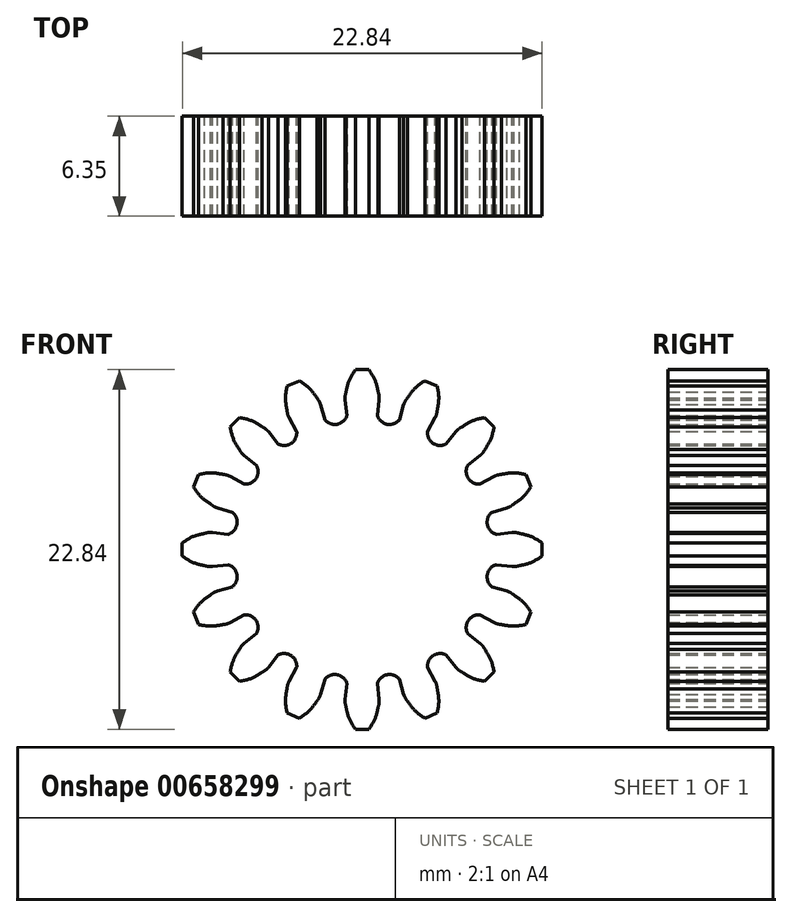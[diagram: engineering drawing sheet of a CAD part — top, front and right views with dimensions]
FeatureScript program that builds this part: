
annotation { "Feature Type Name" : "Feature", "Feature Type Description" : "" }
export const myFeature = defineFeature(function(context is Context, id is Id, definition is map)
    precondition{}
    {
        {
            var Q0;
            Q0=qCreatedBy(makeId("Front.planeOp"),FACE);
            var sketch = newSketch(context, id + "F0", { "sketchPlane" : qUnion([Q0])});
            skLineSegment(sketch, "E0", {"start": v(8.52, -0.97) * mm, "end": v(9.5, -1.08) * mm});
            skFitSpline(sketch, "E1", {"points": [v(9.5, -1.08) * mm, v(9.56, -1.08) * mm, v(9.73, -1.08) * mm, v(10, -1.02) * mm]});
            skFitSpline(sketch, "E2", {"points": [v(10, -1.02) * mm, v(10.34, -0.95) * mm, v(10.83, -0.78) * mm, v(11.42, -0.42) * mm]});
            skLineSegment(sketch, "E3", {"start": v(11.42, -0.42) * mm, "end": v(11.42, 0.42) * mm});
            skFitSpline(sketch, "E4", {"points": [v(11.42, 0.42) * mm, v(10.83, 0.78) * mm, v(10.34, 0.95) * mm, v(10, 1.02) * mm]});
            skFitSpline(sketch, "E5", {"points": [v(10, 1.02) * mm, v(9.73, 1.08) * mm, v(9.56, 1.08) * mm, v(9.5, 1.08) * mm]});
            skLineSegment(sketch, "E6", {"start": v(9.5, 1.08) * mm, "end": v(8.52, 0.97) * mm});
            skArc(sketch, "E7", {"start": v(8.24, 2.37) * mm, "mid": v(7.95, 1.58) * mm, "end": v(8.52, 0.97) * mm});
            skLineSegment(sketch, "E8", {"start": v(8.24, 2.37) * mm, "end": v(9.2, 2.64) * mm});
            skFitSpline(sketch, "E9", {"points": [v(9.2, 2.64) * mm, v(9.25, 2.66) * mm, v(9.4, 2.72) * mm, v(9.63, 2.88) * mm]});
            skFitSpline(sketch, "E10", {"points": [v(9.63, 2.88) * mm, v(9.91, 3.08) * mm, v(10.3, 3.42) * mm, v(10.72, 3.98) * mm]});
            skLineSegment(sketch, "E11", {"start": v(10.72, 3.98) * mm, "end": v(10.4, 4.76) * mm});
            skFitSpline(sketch, "E12", {"points": [v(10.4, 4.76) * mm, v(9.7, 4.87) * mm, v(9.19, 4.83) * mm, v(8.85, 4.77) * mm]});
            skFitSpline(sketch, "E13", {"points": [v(8.85, 4.77) * mm, v(8.57, 4.72) * mm, v(8.42, 4.66) * mm, v(8.37, 4.64) * mm]});
            skLineSegment(sketch, "E14", {"start": v(8.37, 4.64) * mm, "end": v(7.5, 4.15) * mm});
            skArc(sketch, "E15", {"start": v(6.7, 5.34) * mm, "mid": v(6.74, 4.5) * mm, "end": v(7.5, 4.15) * mm});
            skLineSegment(sketch, "E16", {"start": v(6.7, 5.34) * mm, "end": v(7.49, 5.96) * mm});
            skFitSpline(sketch, "E17", {"points": [v(7.49, 5.96) * mm, v(7.53, 6) * mm, v(7.64, 6.11) * mm, v(7.8, 6.35) * mm]});
            skFitSpline(sketch, "E18", {"points": [v(7.8, 6.35) * mm, v(7.98, 6.64) * mm, v(8.2, 7.1) * mm, v(8.38, 7.78) * mm]});
            skLineSegment(sketch, "E19", {"start": v(8.38, 7.78) * mm, "end": v(7.78, 8.38) * mm});
            skFitSpline(sketch, "E20", {"points": [v(7.78, 8.38) * mm, v(7.1, 8.2) * mm, v(6.64, 7.98) * mm, v(6.35, 7.8) * mm]});
            skFitSpline(sketch, "E21", {"points": [v(6.35, 7.8) * mm, v(6.11, 7.64) * mm, v(6, 7.53) * mm, v(5.96, 7.49) * mm]});
            skLineSegment(sketch, "E22", {"start": v(5.96, 7.49) * mm, "end": v(5.34, 6.7) * mm});
            skArc(sketch, "E23", {"start": v(4.15, 7.5) * mm, "mid": v(4.5, 6.74) * mm, "end": v(5.34, 6.7) * mm});
            skLineSegment(sketch, "E24", {"start": v(4.15, 7.5) * mm, "end": v(4.64, 8.37) * mm});
            skFitSpline(sketch, "E25", {"points": [v(4.64, 8.37) * mm, v(4.66, 8.42) * mm, v(4.72, 8.57) * mm, v(4.77, 8.85) * mm]});
            skFitSpline(sketch, "E26", {"points": [v(4.77, 8.85) * mm, v(4.83, 9.19) * mm, v(4.87, 9.7) * mm, v(4.76, 10.4) * mm]});
            skLineSegment(sketch, "E27", {"start": v(4.76, 10.4) * mm, "end": v(3.98, 10.72) * mm});
            skFitSpline(sketch, "E28", {"points": [v(3.98, 10.72) * mm, v(3.42, 10.3) * mm, v(3.08, 9.91) * mm, v(2.88, 9.63) * mm]});
            skFitSpline(sketch, "E29", {"points": [v(2.88, 9.63) * mm, v(2.72, 9.4) * mm, v(2.66, 9.25) * mm, v(2.64, 9.2) * mm]});
            skLineSegment(sketch, "E30", {"start": v(2.64, 9.2) * mm, "end": v(2.37, 8.24) * mm});
            skArc(sketch, "E31", {"start": v(0.97, 8.52) * mm, "mid": v(1.58, 7.95) * mm, "end": v(2.37, 8.24) * mm});
            skLineSegment(sketch, "E32", {"start": v(0.97, 8.52) * mm, "end": v(1.08, 9.5) * mm});
            skFitSpline(sketch, "E33", {"points": [v(1.08, 9.5) * mm, v(1.08, 9.56) * mm, v(1.08, 9.73) * mm, v(1.02, 10) * mm]});
            skFitSpline(sketch, "E34", {"points": [v(1.02, 10) * mm, v(0.95, 10.34) * mm, v(0.78, 10.83) * mm, v(0.42, 11.42) * mm]});
            skLineSegment(sketch, "E35", {"start": v(0.42, 11.42) * mm, "end": v(-0.42, 11.42) * mm});
            skFitSpline(sketch, "E36", {"points": [v(-0.42, 11.42) * mm, v(-0.78, 10.83) * mm, v(-0.95, 10.34) * mm, v(-1.02, 10) * mm]});
            skFitSpline(sketch, "E37", {"points": [v(-1.02, 10) * mm, v(-1.08, 9.73) * mm, v(-1.08, 9.56) * mm, v(-1.08, 9.5) * mm]});
            skLineSegment(sketch, "E38", {"start": v(-1.08, 9.5) * mm, "end": v(-0.97, 8.52) * mm});
            skArc(sketch, "E39", {"start": v(-2.37, 8.24) * mm, "mid": v(-1.58, 7.95) * mm, "end": v(-0.97, 8.52) * mm});
            skLineSegment(sketch, "E40", {"start": v(-2.37, 8.24) * mm, "end": v(-2.64, 9.2) * mm});
            skFitSpline(sketch, "E41", {"points": [v(-2.64, 9.2) * mm, v(-2.66, 9.25) * mm, v(-2.72, 9.4) * mm, v(-2.88, 9.63) * mm]});
            skFitSpline(sketch, "E42", {"points": [v(-2.88, 9.63) * mm, v(-3.08, 9.91) * mm, v(-3.42, 10.3) * mm, v(-3.98, 10.72) * mm]});
            skLineSegment(sketch, "E43", {"start": v(-3.98, 10.72) * mm, "end": v(-4.76, 10.4) * mm});
            skFitSpline(sketch, "E44", {"points": [v(-4.76, 10.4) * mm, v(-4.87, 9.7) * mm, v(-4.83, 9.19) * mm, v(-4.77, 8.85) * mm]});
            skFitSpline(sketch, "E45", {"points": [v(-4.77, 8.85) * mm, v(-4.72, 8.57) * mm, v(-4.66, 8.42) * mm, v(-4.64, 8.37) * mm]});
            skLineSegment(sketch, "E46", {"start": v(-4.64, 8.37) * mm, "end": v(-4.15, 7.5) * mm});
            skArc(sketch, "E47", {"start": v(-5.34, 6.7) * mm, "mid": v(-4.5, 6.74) * mm, "end": v(-4.15, 7.5) * mm});
            skLineSegment(sketch, "E48", {"start": v(-5.34, 6.7) * mm, "end": v(-5.96, 7.49) * mm});
            skFitSpline(sketch, "E49", {"points": [v(-5.96, 7.49) * mm, v(-6, 7.53) * mm, v(-6.11, 7.64) * mm, v(-6.35, 7.8) * mm]});
            skFitSpline(sketch, "E50", {"points": [v(-6.35, 7.8) * mm, v(-6.64, 7.98) * mm, v(-7.1, 8.2) * mm, v(-7.78, 8.38) * mm]});
            skLineSegment(sketch, "E51", {"start": v(-7.78, 8.38) * mm, "end": v(-8.38, 7.78) * mm});
            skFitSpline(sketch, "E52", {"points": [v(-8.38, 7.78) * mm, v(-8.2, 7.1) * mm, v(-7.98, 6.64) * mm, v(-7.8, 6.35) * mm]});
            skFitSpline(sketch, "E53", {"points": [v(-7.8, 6.35) * mm, v(-7.64, 6.11) * mm, v(-7.53, 6) * mm, v(-7.49, 5.96) * mm]});
            skLineSegment(sketch, "E54", {"start": v(-7.49, 5.96) * mm, "end": v(-6.7, 5.34) * mm});
            skArc(sketch, "E55", {"start": v(-7.5, 4.15) * mm, "mid": v(-6.74, 4.5) * mm, "end": v(-6.7, 5.34) * mm});
            skLineSegment(sketch, "E56", {"start": v(-7.5, 4.15) * mm, "end": v(-8.37, 4.64) * mm});
            skFitSpline(sketch, "E57", {"points": [v(-8.37, 4.64) * mm, v(-8.42, 4.66) * mm, v(-8.57, 4.72) * mm, v(-8.85, 4.77) * mm]});
            skFitSpline(sketch, "E58", {"points": [v(-8.85, 4.77) * mm, v(-9.19, 4.83) * mm, v(-9.7, 4.87) * mm, v(-10.4, 4.76) * mm]});
            skLineSegment(sketch, "E59", {"start": v(-10.4, 4.76) * mm, "end": v(-10.72, 3.98) * mm});
            skFitSpline(sketch, "E60", {"points": [v(-10.72, 3.98) * mm, v(-10.3, 3.42) * mm, v(-9.91, 3.08) * mm, v(-9.63, 2.88) * mm]});
            skFitSpline(sketch, "E61", {"points": [v(-9.63, 2.88) * mm, v(-9.4, 2.72) * mm, v(-9.25, 2.66) * mm, v(-9.2, 2.64) * mm]});
            skLineSegment(sketch, "E62", {"start": v(-9.2, 2.64) * mm, "end": v(-8.24, 2.37) * mm});
            skArc(sketch, "E63", {"start": v(-8.52, 0.97) * mm, "mid": v(-7.95, 1.58) * mm, "end": v(-8.24, 2.37) * mm});
            skLineSegment(sketch, "E64", {"start": v(-8.52, 0.97) * mm, "end": v(-9.5, 1.08) * mm});
            skFitSpline(sketch, "E65", {"points": [v(-9.5, 1.08) * mm, v(-9.56, 1.08) * mm, v(-9.73, 1.08) * mm, v(-10, 1.02) * mm]});
            skFitSpline(sketch, "E66", {"points": [v(-10, 1.02) * mm, v(-10.34, 0.95) * mm, v(-10.83, 0.78) * mm, v(-11.42, 0.42) * mm]});
            skLineSegment(sketch, "E67", {"start": v(-11.42, 0.42) * mm, "end": v(-11.42, -0.42) * mm});
            skFitSpline(sketch, "E68", {"points": [v(-11.42, -0.42) * mm, v(-10.83, -0.78) * mm, v(-10.34, -0.95) * mm, v(-10, -1.02) * mm]});
            skFitSpline(sketch, "E69", {"points": [v(-10, -1.02) * mm, v(-9.73, -1.08) * mm, v(-9.56, -1.08) * mm, v(-9.5, -1.08) * mm]});
            skLineSegment(sketch, "E70", {"start": v(-9.5, -1.08) * mm, "end": v(-8.52, -0.97) * mm});
            skArc(sketch, "E71", {"start": v(-8.24, -2.37) * mm, "mid": v(-7.95, -1.58) * mm, "end": v(-8.52, -0.97) * mm});
            skLineSegment(sketch, "E72", {"start": v(-8.24, -2.37) * mm, "end": v(-9.2, -2.64) * mm});
            skFitSpline(sketch, "E73", {"points": [v(-9.2, -2.64) * mm, v(-9.25, -2.66) * mm, v(-9.4, -2.72) * mm, v(-9.63, -2.88) * mm]});
            skFitSpline(sketch, "E74", {"points": [v(-9.63, -2.88) * mm, v(-9.91, -3.08) * mm, v(-10.3, -3.42) * mm, v(-10.72, -3.98) * mm]});
            skLineSegment(sketch, "E75", {"start": v(-10.72, -3.98) * mm, "end": v(-10.4, -4.76) * mm});
            skFitSpline(sketch, "E76", {"points": [v(-10.4, -4.76) * mm, v(-9.7, -4.87) * mm, v(-9.19, -4.83) * mm, v(-8.85, -4.77) * mm]});
            skFitSpline(sketch, "E77", {"points": [v(-8.85, -4.77) * mm, v(-8.57, -4.72) * mm, v(-8.42, -4.66) * mm, v(-8.37, -4.64) * mm]});
            skLineSegment(sketch, "E78", {"start": v(-8.37, -4.64) * mm, "end": v(-7.5, -4.15) * mm});
            skArc(sketch, "E79", {"start": v(-6.7, -5.34) * mm, "mid": v(-6.74, -4.5) * mm, "end": v(-7.5, -4.15) * mm});
            skLineSegment(sketch, "E80", {"start": v(-6.7, -5.34) * mm, "end": v(-7.49, -5.96) * mm});
            skFitSpline(sketch, "E81", {"points": [v(-7.49, -5.96) * mm, v(-7.53, -6) * mm, v(-7.64, -6.11) * mm, v(-7.8, -6.35) * mm]});
            skFitSpline(sketch, "E82", {"points": [v(-7.8, -6.35) * mm, v(-7.98, -6.64) * mm, v(-8.2, -7.1) * mm, v(-8.38, -7.78) * mm]});
            skLineSegment(sketch, "E83", {"start": v(-8.38, -7.78) * mm, "end": v(-7.78, -8.38) * mm});
            skFitSpline(sketch, "E84", {"points": [v(-7.78, -8.38) * mm, v(-7.1, -8.2) * mm, v(-6.64, -7.98) * mm, v(-6.35, -7.8) * mm]});
            skFitSpline(sketch, "E85", {"points": [v(-6.35, -7.8) * mm, v(-6.11, -7.64) * mm, v(-6, -7.53) * mm, v(-5.96, -7.49) * mm]});
            skLineSegment(sketch, "E86", {"start": v(-5.96, -7.49) * mm, "end": v(-5.34, -6.7) * mm});
            skArc(sketch, "E87", {"start": v(-4.15, -7.5) * mm, "mid": v(-4.5, -6.74) * mm, "end": v(-5.34, -6.7) * mm});
            skLineSegment(sketch, "E88", {"start": v(-4.15, -7.5) * mm, "end": v(-4.64, -8.37) * mm});
            skFitSpline(sketch, "E89", {"points": [v(-4.64, -8.37) * mm, v(-4.66, -8.42) * mm, v(-4.72, -8.57) * mm, v(-4.77, -8.85) * mm]});
            skFitSpline(sketch, "E90", {"points": [v(-4.77, -8.85) * mm, v(-4.83, -9.19) * mm, v(-4.87, -9.7) * mm, v(-4.76, -10.4) * mm]});
            skLineSegment(sketch, "E91", {"start": v(-4.76, -10.4) * mm, "end": v(-3.98, -10.72) * mm});
            skFitSpline(sketch, "E92", {"points": [v(-3.98, -10.72) * mm, v(-3.42, -10.3) * mm, v(-3.08, -9.91) * mm, v(-2.88, -9.63) * mm]});
            skFitSpline(sketch, "E93", {"points": [v(-2.88, -9.63) * mm, v(-2.72, -9.4) * mm, v(-2.66, -9.25) * mm, v(-2.64, -9.2) * mm]});
            skLineSegment(sketch, "E94", {"start": v(-2.64, -9.2) * mm, "end": v(-2.37, -8.24) * mm});
            skArc(sketch, "E95", {"start": v(-0.97, -8.52) * mm, "mid": v(-1.58, -7.95) * mm, "end": v(-2.37, -8.24) * mm});
            skLineSegment(sketch, "E96", {"start": v(-0.97, -8.52) * mm, "end": v(-1.08, -9.5) * mm});
            skFitSpline(sketch, "E97", {"points": [v(-1.08, -9.5) * mm, v(-1.08, -9.56) * mm, v(-1.08, -9.73) * mm, v(-1.02, -10) * mm]});
            skFitSpline(sketch, "E98", {"points": [v(-1.02, -10) * mm, v(-0.95, -10.34) * mm, v(-0.78, -10.83) * mm, v(-0.42, -11.42) * mm]});
            skLineSegment(sketch, "E99", {"start": v(-0.42, -11.42) * mm, "end": v(0.42, -11.42) * mm});
            skFitSpline(sketch, "E100", {"points": [v(0.42, -11.42) * mm, v(0.78, -10.83) * mm, v(0.95, -10.34) * mm, v(1.02, -10) * mm]});
            skFitSpline(sketch, "E101", {"points": [v(1.02, -10) * mm, v(1.08, -9.73) * mm, v(1.08, -9.56) * mm, v(1.08, -9.5) * mm]});
            skLineSegment(sketch, "E102", {"start": v(1.08, -9.5) * mm, "end": v(0.97, -8.52) * mm});
            skArc(sketch, "E103", {"start": v(2.37, -8.24) * mm, "mid": v(1.58, -7.95) * mm, "end": v(0.97, -8.52) * mm});
            skLineSegment(sketch, "E104", {"start": v(2.37, -8.24) * mm, "end": v(2.64, -9.2) * mm});
            skFitSpline(sketch, "E105", {"points": [v(2.64, -9.2) * mm, v(2.66, -9.25) * mm, v(2.72, -9.4) * mm, v(2.88, -9.63) * mm]});
            skFitSpline(sketch, "E106", {"points": [v(2.88, -9.63) * mm, v(3.08, -9.91) * mm, v(3.42, -10.3) * mm, v(3.98, -10.72) * mm]});
            skLineSegment(sketch, "E107", {"start": v(3.98, -10.72) * mm, "end": v(4.76, -10.4) * mm});
            skFitSpline(sketch, "E108", {"points": [v(4.76, -10.4) * mm, v(4.87, -9.7) * mm, v(4.83, -9.19) * mm, v(4.77, -8.85) * mm]});
            skFitSpline(sketch, "E109", {"points": [v(4.77, -8.85) * mm, v(4.72, -8.57) * mm, v(4.66, -8.42) * mm, v(4.64, -8.37) * mm]});
            skLineSegment(sketch, "E110", {"start": v(4.64, -8.37) * mm, "end": v(4.15, -7.5) * mm});
            skArc(sketch, "E111", {"start": v(5.34, -6.7) * mm, "mid": v(4.5, -6.74) * mm, "end": v(4.15, -7.5) * mm});
            skLineSegment(sketch, "E112", {"start": v(5.34, -6.7) * mm, "end": v(5.96, -7.49) * mm});
            skFitSpline(sketch, "E113", {"points": [v(5.96, -7.49) * mm, v(6, -7.53) * mm, v(6.11, -7.64) * mm, v(6.35, -7.8) * mm]});
            skFitSpline(sketch, "E114", {"points": [v(6.35, -7.8) * mm, v(6.64, -7.98) * mm, v(7.1, -8.2) * mm, v(7.78, -8.38) * mm]});
            skLineSegment(sketch, "E115", {"start": v(7.78, -8.38) * mm, "end": v(8.38, -7.78) * mm});
            skFitSpline(sketch, "E116", {"points": [v(8.38, -7.78) * mm, v(8.2, -7.1) * mm, v(7.98, -6.64) * mm, v(7.8, -6.35) * mm]});
            skFitSpline(sketch, "E117", {"points": [v(7.8, -6.35) * mm, v(7.64, -6.11) * mm, v(7.53, -6) * mm, v(7.49, -5.96) * mm]});
            skLineSegment(sketch, "E118", {"start": v(7.49, -5.96) * mm, "end": v(6.7, -5.34) * mm});
            skArc(sketch, "E119", {"start": v(7.5, -4.15) * mm, "mid": v(6.74, -4.5) * mm, "end": v(6.7, -5.34) * mm});
            skLineSegment(sketch, "E120", {"start": v(7.5, -4.15) * mm, "end": v(8.37, -4.64) * mm});
            skFitSpline(sketch, "E121", {"points": [v(8.37, -4.64) * mm, v(8.42, -4.66) * mm, v(8.57, -4.72) * mm, v(8.85, -4.77) * mm]});
            skFitSpline(sketch, "E122", {"points": [v(8.85, -4.77) * mm, v(9.19, -4.83) * mm, v(9.7, -4.87) * mm, v(10.4, -4.76) * mm]});
            skLineSegment(sketch, "E123", {"start": v(10.4, -4.76) * mm, "end": v(10.72, -3.98) * mm});
            skFitSpline(sketch, "E124", {"points": [v(10.72, -3.98) * mm, v(10.3, -3.42) * mm, v(9.91, -3.08) * mm, v(9.63, -2.88) * mm]});
            skFitSpline(sketch, "E125", {"points": [v(9.63, -2.88) * mm, v(9.4, -2.72) * mm, v(9.25, -2.66) * mm, v(9.2, -2.64) * mm]});
            skLineSegment(sketch, "E126", {"start": v(9.2, -2.64) * mm, "end": v(8.24, -2.37) * mm});
            skArc(sketch, "E127", {"start": v(8.52, -0.97) * mm, "mid": v(7.95, -1.58) * mm, "end": v(8.24, -2.37) * mm});
            skSolve(sketch);
        }
        {
            var Q0;
            Q0=makeQuery(id+"F0.imprint","IMPRINT",FACE,{"disambiguationData":[TD([[makeQuery(id+"F0.imprint","IMPRINT",EDGE,{"derivedFrom":sQuery(id+"F0.wireOp",EDGE,"E0")}),1.0]])]});
            extrude(context, id + "F1", {"entities" : qUnion([Q0]), "depth" : 6.35 * mm, "offsetDistance" : 25.4 * mm});
        }
    });
